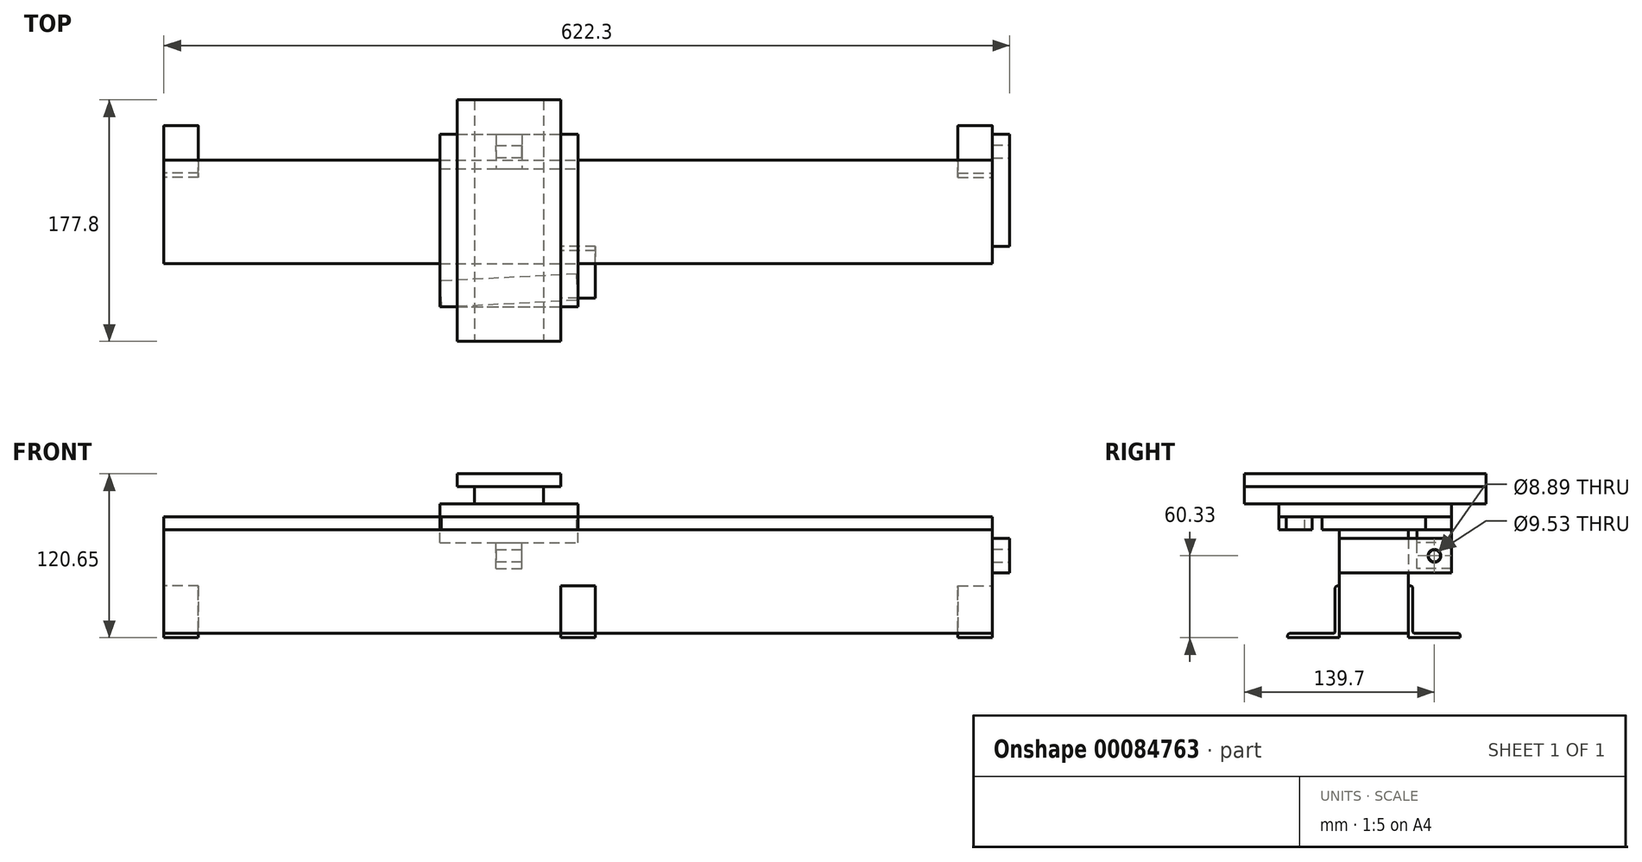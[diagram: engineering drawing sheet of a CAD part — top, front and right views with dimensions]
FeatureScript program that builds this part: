
annotation { "Feature Type Name" : "Feature", "Feature Type Description" : "" }
export const myFeature = defineFeature(function(context is Context, id is Id, definition is map)
    precondition{}
    {
        {
            var Q0;
            Q0=qCreatedBy(makeId("Right.planeOp"),FACE);
            var sketch = newSketch(context, id + "F0", { "sketchPlane" : qUnion([Q0])});
            skLineSegment(sketch, "E0.bottom", {"start": v(-25.4, 0) * mm, "end": v(25.4, 0) * mm});
            skLineSegment(sketch, "E0.top", {"start": v(-25.4, -76.2) * mm, "end": v(25.4, -76.2) * mm});
            skLineSegment(sketch, "E0.left", {"start": v(-25.4, 0) * mm, "end": v(-25.4, -76.2) * mm});
            skLineSegment(sketch, "E0.right", {"start": v(25.4, 0) * mm, "end": v(25.4, -76.2) * mm});
            skSolve(sketch);
        }
        {
            var Q0;
            Q0 = qSketchRegion(id + "F0", true);
            extrude(context, id + "F1", {"entities" : qUnion([Q0]), "endBound" : BoundingType.SYMMETRIC, "depth" : 609.6 * mm});
        }
        {
            var Q0;
            Q0=makeQuery(id+"F1.opExtrude","SWEPT_FACE",FACE,{"disambiguationData":[OSD([sQuery(id+"F0.wireOp",EDGE,"E0.bottom")])]});
            var sketch = newSketch(context, id + "F2", { "sketchPlane" : qUnion([Q0])});
            skLineSegment(sketch, "E1.bottom", {"start": v(-304.8, 38.1) * mm, "end": v(304.8, 38.1) * mm});
            skLineSegment(sketch, "E1.top", {"start": v(-304.8, -38.1) * mm, "end": v(304.8, -38.1) * mm});
            skLineSegment(sketch, "E1.left", {"start": v(-304.8, 38.1) * mm, "end": v(-304.8, -38.1) * mm});
            skLineSegment(sketch, "E1.right", {"start": v(304.8, 38.1) * mm, "end": v(304.8, -38.1) * mm});
            skSolve(sketch);
        }
        {
            var Q0;
            Q0 = qSketchRegion(id + "F2", true);
            extrude(context, id + "F3", {"entities" : qUnion([Q0]), "depth" : 9.52 * mm});
        }
        {
            var Q0;
            Q0=makeQuery(id+"F1.opExtrude","CAP_FACE",FACE,{"disambiguationData":[OSD([sQuery(id+"F0.wireOp",EDGE,"E0.bottom"),sQuery(id+"F0.wireOp",EDGE,"E0.top"),sQuery(id+"F0.wireOp",EDGE,"E0.left"),sQuery(id+"F0.wireOp",EDGE,"E0.right")])],"isStart":true});
            var sketch = newSketch(context, id + "F4", { "sketchPlane" : qUnion([Q0])});
            skLineSegment(sketch, "E2", {"start": v(25.4, -41.27) * mm, "end": v(25.4, -79.38) * mm});
            skLineSegment(sketch, "E3", {"start": v(25.4, -79.38) * mm, "end": v(63.5, -79.38) * mm});
            skLineSegment(sketch, "E4", {"start": v(63.5, -79.38) * mm, "end": v(63.5, -77.72) * mm});
            skLineSegment(sketch, "E5", {"start": v(61.98, -76.2) * mm, "end": v(30.1, -76.2) * mm});
            skLineSegment(sketch, "E6", {"start": v(28.58, -74.68) * mm, "end": v(28.57, -42.8) * mm});
            skLineSegment(sketch, "E7", {"start": v(27.05, -41.27) * mm, "end": v(25.4, -41.27) * mm});
            skPoint(sketch, "E8.visualSharp", {"position": v(28.57, -41.27) * mm});
            skArc(sketch, "E8.filletArc", {"start": v(28.57, -42.8) * mm, "mid": v(28.13, -41.72) * mm, "end": v(27.05, -41.27) * mm});
            skPoint(sketch, "E9.visualSharp", {"position": v(28.58, -76.2) * mm});
            skArc(sketch, "E9.filletArc", {"start": v(28.58, -74.68) * mm, "mid": v(29.02, -75.75) * mm, "end": v(30.1, -76.2) * mm});
            skPoint(sketch, "E10.visualSharp", {"position": v(63.5, -76.2) * mm});
            skArc(sketch, "E10.filletArc", {"start": v(63.5, -77.72) * mm, "mid": v(63.05, -76.65) * mm, "end": v(61.98, -76.2) * mm});
            skSolve(sketch);
        }
        {
            var Q0;
            {var subQ0=sQuery(id+"F4.wireOp",EDGE,"E3");Q0=makeQuery(id+"F4.imprint","IMPRINT",FACE,{"disambiguationData":[TD([[makeQuery(id+"F4.imprint","IMPRINT",EDGE,{"derivedFrom":subQ0}),1.0]])]});}
            extrude(context, id + "F5", {"entities" : qUnion([Q0]), "oppositeDirection" : true, "depth" : 25.4 * mm});
        }
        {
            var Q0;
            Q0=makeQuery(id+"F5.opExtrude","SWEPT_BODY",BODY,{"disambiguationData":[OSD([sQuery(id+"F4.wireOp",EDGE,"E2"),sQuery(id+"F4.wireOp",EDGE,"E3"),sQuery(id+"F4.wireOp",EDGE,"E4"),sQuery(id+"F4.wireOp",EDGE,"E5"),sQuery(id+"F4.wireOp",EDGE,"E6"),sQuery(id+"F4.wireOp",EDGE,"E7"),sQuery(id+"F4.wireOp",EDGE,"E8.filletArc"),sQuery(id+"F4.wireOp",EDGE,"E9.filletArc"),sQuery(id+"F4.wireOp",EDGE,"E10.filletArc")])]});
            transform(context, id + "F6", {"entities" : qUnion([Q0]), "transformType" : TransformType.TRANSLATION_3D, "dx" : 292.1 * mm, "dy" : 0 * mm, "dz" : 0 * mm, "makeCopy" : true});
        }
        {
            var Q0;
            Q0=qCreatedBy(makeId("Front.planeOp"),FACE);
            var sketch = newSketch(context, id + "F7", { "sketchPlane" : qUnion([Q0])});
            skLineSegment(sketch, "E11", {"start": v(0, 0) * mm, "end": v(0, 108.77) * mm});
            skSolve(sketch);
        }
        {
            var Q0;
            Q0=makeQuery(id+"F6.opPattern","COPY",BODY,{"derivedFrom":makeQuery(id+"F5.opExtrude","SWEPT_BODY",BODY,{"disambiguationData":[OSD([sQuery(id+"F4.wireOp",EDGE,"E2"),sQuery(id+"F4.wireOp",EDGE,"E3"),sQuery(id+"F4.wireOp",EDGE,"E4"),sQuery(id+"F4.wireOp",EDGE,"E5"),sQuery(id+"F4.wireOp",EDGE,"E6"),sQuery(id+"F4.wireOp",EDGE,"E7"),sQuery(id+"F4.wireOp",EDGE,"E8.filletArc"),sQuery(id+"F4.wireOp",EDGE,"E9.filletArc"),sQuery(id+"F4.wireOp",EDGE,"E10.filletArc")])]}),"instanceName":"1"});
            var Q1;
            Q1=sQuery(id+"F7.wireOp",EDGE,"E11");
            transform(context, id + "F8", {"entities" : qUnion([Q0]), "transformType" : TransformType.ROTATION, "transformAxis" : qUnion([Q1]), "angle" : 180 * degree, "makeCopy" : false});
        }
        {
            var Q0;
            Q0=makeQuery(id+"F5.opExtrude","SWEPT_BODY",BODY,{"disambiguationData":[OSD([sQuery(id+"F4.wireOp",EDGE,"E2"),sQuery(id+"F4.wireOp",EDGE,"E3"),sQuery(id+"F4.wireOp",EDGE,"E4"),sQuery(id+"F4.wireOp",EDGE,"E5"),sQuery(id+"F4.wireOp",EDGE,"E6"),sQuery(id+"F4.wireOp",EDGE,"E7"),sQuery(id+"F4.wireOp",EDGE,"E8.filletArc"),sQuery(id+"F4.wireOp",EDGE,"E9.filletArc"),sQuery(id+"F4.wireOp",EDGE,"E10.filletArc")])]});
            var Q1;
            Q1=qCreatedBy(makeId("Right.planeOp"),FACE);
            mirror(context, id + "F9", {"entities" : qUnion([Q0]), "mirrorPlane" : qUnion([Q1])});
        }
        {
            var Q0;
            Q0=makeQuery(id+"F9.opPattern","COPY",BODY,{"derivedFrom":makeQuery(id+"F5.opExtrude","SWEPT_BODY",BODY,{"disambiguationData":[OSD([sQuery(id+"F4.wireOp",EDGE,"E2"),sQuery(id+"F4.wireOp",EDGE,"E3"),sQuery(id+"F4.wireOp",EDGE,"E4"),sQuery(id+"F4.wireOp",EDGE,"E5"),sQuery(id+"F4.wireOp",EDGE,"E6"),sQuery(id+"F4.wireOp",EDGE,"E7"),sQuery(id+"F4.wireOp",EDGE,"E8.filletArc"),sQuery(id+"F4.wireOp",EDGE,"E9.filletArc"),sQuery(id+"F4.wireOp",EDGE,"E10.filletArc")])]}),"instanceName":"1"});
            var Q1;
            Q1=makeQuery(id+"F6.opPattern","COPY",BODY,{"derivedFrom":makeQuery(id+"F5.opExtrude","SWEPT_BODY",BODY,{"disambiguationData":[OSD([sQuery(id+"F4.wireOp",EDGE,"E2"),sQuery(id+"F4.wireOp",EDGE,"E3"),sQuery(id+"F4.wireOp",EDGE,"E4"),sQuery(id+"F4.wireOp",EDGE,"E5"),sQuery(id+"F4.wireOp",EDGE,"E6"),sQuery(id+"F4.wireOp",EDGE,"E7"),sQuery(id+"F4.wireOp",EDGE,"E8.filletArc"),sQuery(id+"F4.wireOp",EDGE,"E9.filletArc"),sQuery(id+"F4.wireOp",EDGE,"E10.filletArc")])]}),"instanceName":"1"});
            var Q2;
            Q2=makeQuery(id+"F5.opExtrude","SWEPT_BODY",BODY,{"disambiguationData":[OSD([sQuery(id+"F4.wireOp",EDGE,"E2"),sQuery(id+"F4.wireOp",EDGE,"E3"),sQuery(id+"F4.wireOp",EDGE,"E4"),sQuery(id+"F4.wireOp",EDGE,"E5"),sQuery(id+"F4.wireOp",EDGE,"E6"),sQuery(id+"F4.wireOp",EDGE,"E7"),sQuery(id+"F4.wireOp",EDGE,"E8.filletArc"),sQuery(id+"F4.wireOp",EDGE,"E9.filletArc"),sQuery(id+"F4.wireOp",EDGE,"E10.filletArc")])]});
            var Q3;
            Q3=sQuery(id+"F7.wireOp",EDGE,"E11");
            transform(context, id + "F10", {"entities" : qUnion([Q0, Q1, Q2]), "transformType" : TransformType.ROTATION, "transformAxis" : qUnion([Q3]), "angle" : 180 * degree, "makeCopy" : false});
        }
        {
            var Q0;
            Q0=qCreatedBy(makeId("Right.planeOp"),FACE);
            var sketch = newSketch(context, id + "F11", { "sketchPlane" : qUnion([Q0])});
            skLineSegment(sketch, "E12.bottom", {"start": v(57.15, 9.53) * mm, "end": v(-69.85, 9.52) * mm});
            skLineSegment(sketch, "E12.top", {"start": v(57.15, 19.05) * mm, "end": v(-69.85, 19.05) * mm});
            skLineSegment(sketch, "E12.left", {"start": v(57.15, 9.53) * mm, "end": v(57.15, 19.05) * mm});
            skLineSegment(sketch, "E12.right", {"start": v(-69.85, 9.52) * mm, "end": v(-69.85, 19.05) * mm});
            skSolve(sketch);
        }
        {
            var Q0;
            Q0=makeQuery(id+"F11.imprint","IMPRINT",FACE,{"disambiguationData":[TD([[makeQuery(id+"F11.imprint","IMPRINT",EDGE,{"derivedFrom":sQuery(id+"F11.wireOp",EDGE,"E12.bottom")}),-1.0]])]});
            extrude(context, id + "F12", {"entities" : qUnion([Q0]), "oppositeDirection" : true, "depth" : 101.6 * mm});
        }
        {
            var Q0;
            Q0=makeQuery(id+"F12.opExtrude","CAP_FACE",FACE,{"disambiguationData":[OSD([sQuery(id+"F11.wireOp",EDGE,"E12.bottom"),sQuery(id+"F11.wireOp",EDGE,"E12.top"),sQuery(id+"F11.wireOp",EDGE,"E12.left"),sQuery(id+"F11.wireOp",EDGE,"E12.right")])],"isStart":true});
            var sketch = newSketch(context, id + "F13", { "sketchPlane" : qUnion([Q0])});
            skLineSegment(sketch, "E13.bottom", {"start": v(38.1, 9.53) * mm, "end": v(57.15, 9.53) * mm});
            skLineSegment(sketch, "E13.top", {"start": v(38.1, 0) * mm, "end": v(57.15, 0) * mm});
            skLineSegment(sketch, "E13.left", {"start": v(38.1, 9.53) * mm, "end": v(38.1, 0) * mm});
            skLineSegment(sketch, "E13.right", {"start": v(57.15, 9.53) * mm, "end": v(57.15, 0) * mm});
            skSolve(sketch);
        }
        {
            var Q0;
            Q0 = qSketchRegion(id + "F13", true);
            var Q1;
            Q1=makeQuery(id+"F12.opExtrude","CAP_FACE",FACE,{"disambiguationData":[OSD([sQuery(id+"F11.wireOp",EDGE,"E12.bottom"),sQuery(id+"F11.wireOp",EDGE,"E12.top"),sQuery(id+"F11.wireOp",EDGE,"E12.left"),sQuery(id+"F11.wireOp",EDGE,"E12.right")])],"isStart":false});
            extrude(context, id + "F14", {"entities" : qUnion([Q0]), "endBound" : BoundingType.UP_TO_SURFACE, "oppositeDirection" : true, "endBoundEntityFace" : qUnion([Q1]), "depth" : 25.4 * mm});
        }
        {
            var Q0;
            Q0=makeQuery(id+"F12.opExtrude","SWEPT_FACE",FACE,{"disambiguationData":[OSD([sQuery(id+"F11.wireOp",EDGE,"E12.bottom")])]});
            var sketch = newSketch(context, id + "F15", { "sketchPlane" : qUnion([Q0])});
            skLineSegment(sketch, "E14", {"start": v(-101.6, 50.83) * mm, "end": v(-100.6, 69.85) * mm});
            skLineSegment(sketch, "E15", {"start": v(-100.6, 69.85) * mm, "end": v(0, 64.58) * mm});
            skLineSegment(sketch, "E16", {"start": v(0, 64.58) * mm, "end": v(-1, 45.55) * mm});
            skLineSegment(sketch, "E17", {"start": v(-1, 45.55) * mm, "end": v(-101.6, 50.83) * mm});
            skSolve(sketch);
        }
        {
            var Q0;
            Q0 = qSketchRegion(id + "F15", true);
            extrude(context, id + "F16", {"entities" : qUnion([Q0]), "depth" : 9.52 * mm});
        }
        {
            var Q0;
            Q0=makeQuery(id+"F12.opExtrude","SWEPT_FACE",FACE,{"disambiguationData":[OSD([sQuery(id+"F11.wireOp",EDGE,"E12.top")])]});
            var sketch = newSketch(context, id + "F17", { "sketchPlane" : qUnion([Q0])});
            skLineSegment(sketch, "E18.bottom", {"start": v(-76.2, 82.55) * mm, "end": v(-25.4, 82.55) * mm});
            skLineSegment(sketch, "E18.top", {"start": v(-76.2, -95.25) * mm, "end": v(-25.4, -95.25) * mm});
            skLineSegment(sketch, "E18.left", {"start": v(-76.2, 82.55) * mm, "end": v(-76.2, -95.25) * mm});
            skLineSegment(sketch, "E18.right", {"start": v(-25.4, 82.55) * mm, "end": v(-25.4, -95.25) * mm});
            skLineSegment(sketch, "E19", {"start": v(-50.8, 57.15) * mm, "end": v(-50.8, 82.55) * mm});
            skSolve(sketch);
        }
        {
            var Q0;
            Q0 = qSketchRegion(id + "F17", true);
            extrude(context, id + "F18", {"entities" : qUnion([Q0]), "depth" : 12.7 * mm});
        }
        {
            var Q0;
            Q0=makeQuery(id+"F18.opExtrude","SWEPT_FACE",FACE,{"disambiguationData":[OSD([sQuery(id+"F17.wireOp",EDGE,"E18.top")])]});
            var sketch = newSketch(context, id + "F19", { "sketchPlane" : qUnion([Q0])});
            skLineSegment(sketch, "E20.bottom", {"start": v(-88.9, 41.27) * mm, "end": v(-12.7, 41.27) * mm});
            skLineSegment(sketch, "E20.top", {"start": v(-88.9, 31.75) * mm, "end": v(-12.7, 31.75) * mm});
            skLineSegment(sketch, "E20.left", {"start": v(-88.9, 41.27) * mm, "end": v(-88.9, 31.75) * mm});
            skLineSegment(sketch, "E20.right", {"start": v(-12.7, 41.27) * mm, "end": v(-12.7, 31.75) * mm});
            skLineSegment(sketch, "E21", {"start": v(-50.8, 41.27) * mm, "end": v(-50.8, 19.05) * mm});
            skSolve(sketch);
        }
        {
            var Q0;
            Q0 = qSketchRegion(id + "F19", true);
            var Q1;
            Q1=makeQuery(id+"F18.opExtrude","SWEPT_FACE",FACE,{"disambiguationData":[OSD([sQuery(id+"F17.wireOp",EDGE,"E18.bottom")])]});
            extrude(context, id + "F20", {"entities" : qUnion([Q0]), "endBound" : BoundingType.UP_TO_SURFACE, "oppositeDirection" : true, "endBoundEntityFace" : qUnion([Q1]), "depth" : 25.4 * mm});
        }
        {
            var Q0;
            Q0=makeQuery(id+"F14.opExtrude","SWEPT_FACE",FACE,{"disambiguationData":[OSD([sQuery(id+"F13.wireOp",EDGE,"E13.top")])]});
            var sketch = newSketch(context, id + "F21", { "sketchPlane" : qUnion([Q0])});
            skLineSegment(sketch, "E22.bottom", {"start": v(-101.6, -57.15) * mm, "end": v(0, -57.15) * mm});
            skLineSegment(sketch, "E22.top", {"start": v(-101.6, -31.75) * mm, "end": v(0, -31.75) * mm});
            skLineSegment(sketch, "E22.left", {"start": v(-101.6, -57.15) * mm, "end": v(-101.6, -31.75) * mm});
            skLineSegment(sketch, "E22.right", {"start": v(0, -57.15) * mm, "end": v(0, -31.75) * mm});
            skSolve(sketch);
        }
        {
            var Q0;
            {var subQ0=sQuery(id+"F21.wireOp",EDGE,"E22.bottom");Q0=makeQuery(id+"F21.imprint","IMPRINT",FACE,{"disambiguationData":[TD([[makeQuery(id+"F21.imprint","IMPRINT",EDGE,{"derivedFrom":subQ0}),1.0]])]});}
            var Q1;
            {var subQ0=sQuery(id+"F21.wireOp",EDGE,"E22.top");Q1=makeQuery(id+"F21.imprint","IMPRINT",FACE,{"disambiguationData":[TD([[makeQuery(id+"F21.imprint","IMPRINT",EDGE,{"derivedFrom":subQ0}),-1.0]])]});}
            extrude(context, id + "F22", {"entities" : qUnion([Q0, Q1]), "depth" : 9.52 * mm});
        }
        {
            var Q0;
            Q0=makeQuery(id+"F22.opExtrude","CAP_FACE",FACE,{"disambiguationData":[OSD([sQuery(id+"F21.wireOp",EDGE,"E22.bottom"),sQuery(id+"F21.wireOp",EDGE,"E22.top"),sQuery(id+"F21.wireOp",EDGE,"E22.left"),sQuery(id+"F21.wireOp",EDGE,"E22.right")])],"isStart":false});
            var sketch = newSketch(context, id + "F23", { "sketchPlane" : qUnion([Q0])});
            skLineSegment(sketch, "E23", {"start": v(-50.8, -57.15) * mm, "end": v(-50.8, -31.75) * mm, "construction": true});
            skLineSegment(sketch, "E24.bottom", {"start": v(-41.28, -57.15) * mm, "end": v(-60.33, -57.15) * mm});
            skLineSegment(sketch, "E24.top", {"start": v(-41.28, -31.75) * mm, "end": v(-60.33, -31.75) * mm});
            skLineSegment(sketch, "E24.left", {"start": v(-41.28, -57.15) * mm, "end": v(-41.28, -31.75) * mm});
            skLineSegment(sketch, "E24.right", {"start": v(-60.33, -57.15) * mm, "end": v(-60.33, -31.75) * mm});
            skSolve(sketch);
        }
        {
            var Q0;
            Q0 = qSketchRegion(id + "F23", true);
            extrude(context, id + "F24", {"entities" : qUnion([Q0]), "depth" : 19.05 * mm});
        }
        {
            var Q0;
            Q0=makeQuery(id+"F24.opExtrude","SWEPT_FACE",FACE,{"disambiguationData":[OSD([sQuery(id+"F23.wireOp",EDGE,"E24.left")])]});
            var sketch = newSketch(context, id + "F25", { "sketchPlane" : qUnion([Q0])});
            skLineSegment(sketch, "E25", {"start": v(31.75, -28.57) * mm, "end": v(57.15, -9.53) * mm, "construction": true});
            skCircle(sketch, "E26", {"center": v(44.45, -19.05) * mm, "radius": 4.45 * mm});
            skSolve(sketch);
        }
        {
            var Q0;
            Q0=makeQuery(id+"F25.imprint","IMPRINT",FACE,{"disambiguationData":[TD([[makeQuery(id+"F25.imprint","IMPRINT",EDGE,{"derivedFrom":sQuery(id+"F25.wireOp",EDGE,"E26")}),1.0]])]});
            extrude(context, id + "F26", {"entities" : qUnion([Q0]), "operationType" : NewBodyOperationType.REMOVE, "endBound" : BoundingType.UP_TO_NEXT, "oppositeDirection" : true, "depth" : 25.4 * mm});
        }
        {
            var Q0;
            Q0=makeQuery(id+"F1.opExtrude","CAP_FACE",FACE,{"disambiguationData":[OSD([sQuery(id+"F0.wireOp",EDGE,"E0.bottom"),sQuery(id+"F0.wireOp",EDGE,"E0.top"),sQuery(id+"F0.wireOp",EDGE,"E0.left"),sQuery(id+"F0.wireOp",EDGE,"E0.right")])],"isStart":false});
            var sketch = newSketch(context, id + "F27", { "sketchPlane" : qUnion([Q0])});
            skLineSegment(sketch, "E27.bottom", {"start": v(-25.4, -6.35) * mm, "end": v(57.15, -6.35) * mm});
            skLineSegment(sketch, "E27.top", {"start": v(-25.4, -31.75) * mm, "end": v(57.15, -31.75) * mm});
            skLineSegment(sketch, "E27.left", {"start": v(-25.4, -6.35) * mm, "end": v(-25.4, -31.75) * mm});
            skLineSegment(sketch, "E27.right", {"start": v(57.15, -6.35) * mm, "end": v(57.15, -31.75) * mm});
            skLineSegment(sketch, "E28", {"start": v(-25.4, -19.05) * mm, "end": v(44.45, -19.05) * mm});
            skSolve(sketch);
        }
        {
            var Q0;
            Q0 = qSketchRegion(id + "F27", true);
            extrude(context, id + "F28", {"entities" : qUnion([Q0]), "depth" : 12.7 * mm});
        }
        {
            var Q0;
            Q0=makeQuery(id+"F28.opExtrude","CAP_FACE",FACE,{"disambiguationData":[OSD([sQuery(id+"F27.wireOp",EDGE,"E27.bottom"),sQuery(id+"F27.wireOp",EDGE,"E27.top"),sQuery(id+"F27.wireOp",EDGE,"E27.left"),sQuery(id+"F27.wireOp",EDGE,"E27.right")])],"isStart":false});
            var sketch = newSketch(context, id + "F29", { "sketchPlane" : qUnion([Q0])});
            skCircle(sketch, "E29", {"center": v(44.45, -19.05) * mm, "radius": 4.76 * mm});
            skSolve(sketch);
        }
        {
            var Q0;
            Q0 = qSketchRegion(id + "F29", true);
            extrude(context, id + "F30", {"entities" : qUnion([Q0]), "operationType" : NewBodyOperationType.REMOVE, "endBound" : BoundingType.UP_TO_NEXT, "oppositeDirection" : true, "depth" : 25.4 * mm});
        }
    });
